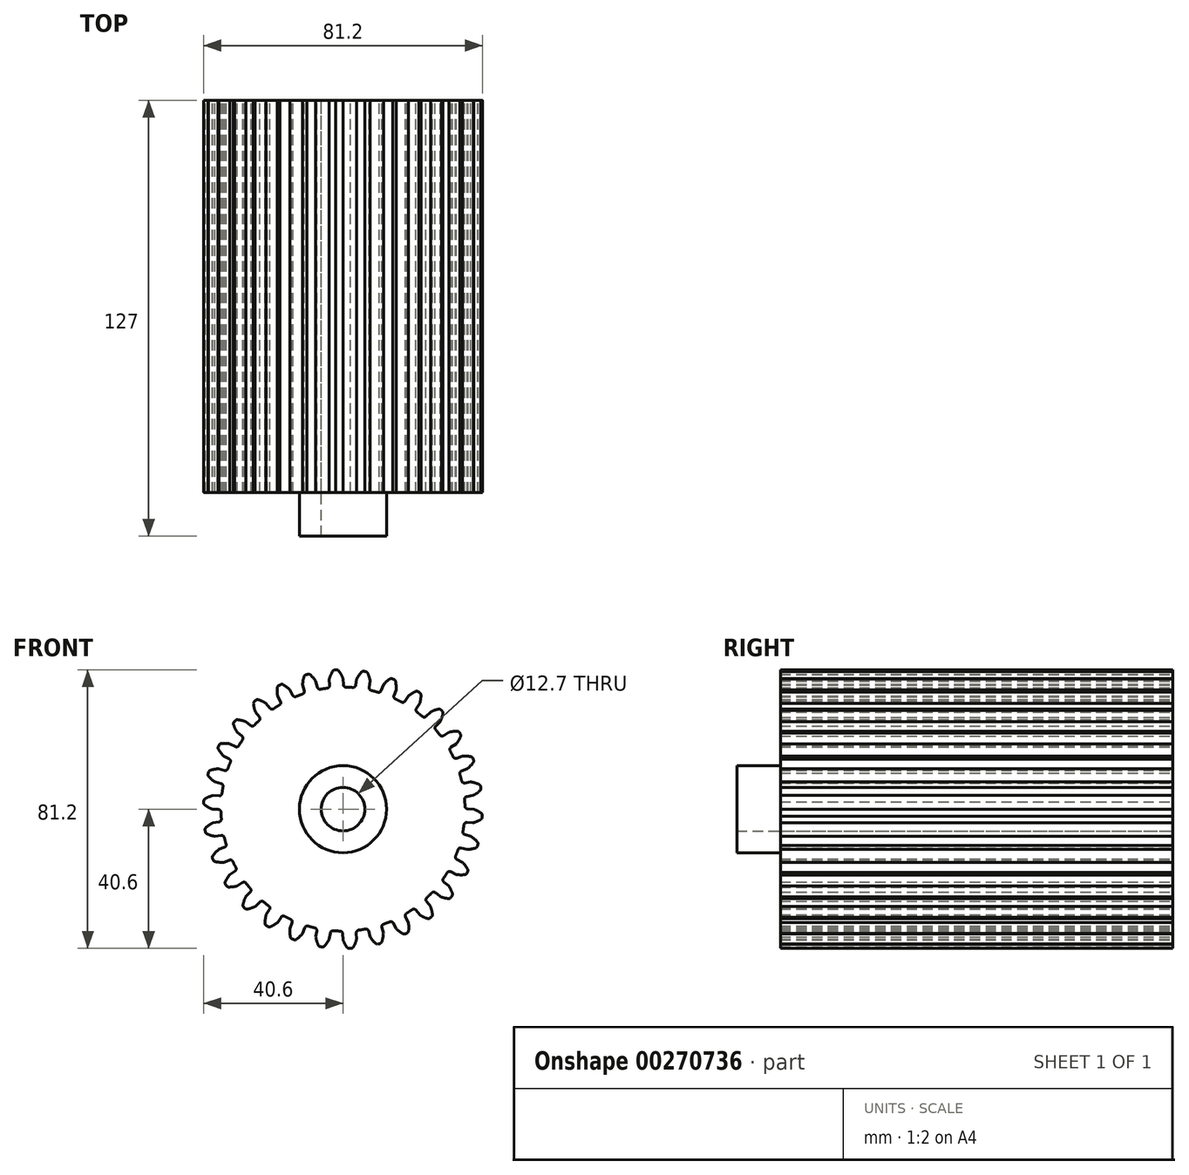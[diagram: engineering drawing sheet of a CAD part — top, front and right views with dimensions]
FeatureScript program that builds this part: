
annotation { "Feature Type Name" : "Feature", "Feature Type Description" : "" }
export const myFeature = defineFeature(function(context is Context, id is Id, definition is map)
    precondition{}
    {
        {
            var Q0;
            Q0=qCreatedBy(makeId("Front.planeOp"),FACE);
            var sketch = newSketch(context, id + "F0", { "sketchPlane" : qUnion([Q0])});
            skArc(sketch, "E0", {"start": v(-4.57, 35.26) * mm, "mid": v(-5.56, 35.12) * mm, "end": v(-6.55, 34.95) * mm});
            skArc(sketch, "E1", {"start": v(0, 38.1) * mm, "mid": v(-0.52, 39.23) * mm, "end": v(-1.18, 40.28) * mm});
            skLineSegment(sketch, "E2", {"start": v(-1.85, 40.6) * mm, "end": v(-2.13, 40.6) * mm});
            skLineSegment(sketch, "E3", {"start": v(0, 38.1) * mm, "end": v(0.1, 36.3) * mm});
            skLineSegment(sketch, "E4.MirrorCS", {"start": v(-2.4, 40.57) * mm, "end": v(-2.13, 40.6) * mm});
            skArc(sketch, "E5.MirrorCS", {"start": v(-3.98, 37.9) * mm, "mid": v(-3.58, 39.07) * mm, "end": v(-3.03, 40.18) * mm});
            skLineSegment(sketch, "E6.MirrorCS", {"start": v(-3.98, 37.9) * mm, "end": v(-3.89, 36.09) * mm});
            skPoint(sketch, "E7.visualSharp", {"position": v(-3.85, 35.35) * mm});
            skArc(sketch, "E7.filletArc", {"start": v(-4.57, 35.26) * mm, "mid": v(-4.07, 35.54) * mm, "end": v(-3.89, 36.09) * mm});
            skPoint(sketch, "E8.visualSharp", {"position": v(0.13, 35.56) * mm});
            skArc(sketch, "E8.filletArc", {"start": v(0.1, 36.3) * mm, "mid": v(0.33, 35.77) * mm, "end": v(0.86, 35.55) * mm});
            skPoint(sketch, "E9.visualSharp", {"position": v(-2.81, 40.54) * mm});
            skArc(sketch, "E9.filletArc", {"start": v(-2.4, 40.57) * mm, "mid": v(-2.77, 40.45) * mm, "end": v(-3.03, 40.18) * mm});
            skPoint(sketch, "E10.visualSharp", {"position": v(-1.44, 40.61) * mm});
            skArc(sketch, "E10.filletArc", {"start": v(-1.18, 40.28) * mm, "mid": v(-1.47, 40.52) * mm, "end": v(-1.85, 40.6) * mm});
            skArc(sketch, "E11.1.0", {"start": v(-11.8, 33.54) * mm, "mid": v(-11.37, 33.92) * mm, "end": v(-11.3, 34.49) * mm});
            skLineSegment(sketch, "E11.1.1", {"start": v(-11.77, 36.24) * mm, "end": v(-11.3, 34.49) * mm});
            skArc(sketch, "E11.1.2", {"start": v(-11.77, 36.24) * mm, "mid": v(-11.63, 37.47) * mm, "end": v(-11.32, 38.67) * mm});
            skArc(sketch, "E11.1.3", {"start": v(-10.79, 39.18) * mm, "mid": v(-11.12, 39) * mm, "end": v(-11.32, 38.67) * mm});
            skLineSegment(sketch, "E11.1.4", {"start": v(-10.79, 39.18) * mm, "end": v(-10.52, 39.26) * mm});
            skLineSegment(sketch, "E11.1.5", {"start": v(-10.25, 39.33) * mm, "end": v(-10.52, 39.26) * mm});
            skArc(sketch, "E11.1.6", {"start": v(-9.53, 39.15) * mm, "mid": v(-9.87, 39.33) * mm, "end": v(-10.25, 39.33) * mm});
            skArc(sketch, "E11.1.7", {"start": v(-7.92, 37.27) * mm, "mid": v(-8.66, 38.26) * mm, "end": v(-9.53, 39.15) * mm});
            skLineSegment(sketch, "E11.1.8", {"start": v(-7.92, 37.27) * mm, "end": v(-7.45, 35.52) * mm});
            skArc(sketch, "E11.1.9", {"start": v(-7.45, 35.52) * mm, "mid": v(-7.11, 35.06) * mm, "end": v(-6.55, 34.95) * mm});
            skArc(sketch, "E11.2.0", {"start": v(-18.52, 30.36) * mm, "mid": v(-18.17, 30.81) * mm, "end": v(-18.23, 31.39) * mm});
            skLineSegment(sketch, "E11.2.1", {"start": v(-19.05, 33) * mm, "end": v(-18.23, 31.39) * mm});
            skArc(sketch, "E11.2.2", {"start": v(-19.05, 33) * mm, "mid": v(-19.16, 34.23) * mm, "end": v(-19.11, 35.47) * mm});
            skArc(sketch, "E11.2.3", {"start": v(-18.7, 36.08) * mm, "mid": v(-18.98, 35.83) * mm, "end": v(-19.11, 35.47) * mm});
            skLineSegment(sketch, "E11.2.4", {"start": v(-18.7, 36.08) * mm, "end": v(-18.45, 36.22) * mm});
            skLineSegment(sketch, "E11.2.5", {"start": v(-18.2, 36.34) * mm, "end": v(-18.45, 36.22) * mm});
            skArc(sketch, "E11.2.6", {"start": v(-17.46, 36.31) * mm, "mid": v(-17.83, 36.42) * mm, "end": v(-18.2, 36.34) * mm});
            skArc(sketch, "E11.2.7", {"start": v(-15.5, 34.8) * mm, "mid": v(-16.43, 35.62) * mm, "end": v(-17.46, 36.31) * mm});
            skLineSegment(sketch, "E11.2.8", {"start": v(-15.5, 34.8) * mm, "end": v(-14.68, 33.2) * mm});
            skArc(sketch, "E11.2.9", {"start": v(-14.68, 33.2) * mm, "mid": v(-14.25, 32.81) * mm, "end": v(-13.67, 32.83) * mm});
            skArc(sketch, "E11.3.0", {"start": v(-24.43, 25.84) * mm, "mid": v(-24.18, 26.36) * mm, "end": v(-24.36, 26.9) * mm});
            skLineSegment(sketch, "E11.3.1", {"start": v(-25.5, 28.31) * mm, "end": v(-24.36, 26.9) * mm});
            skArc(sketch, "E11.3.2", {"start": v(-25.5, 28.31) * mm, "mid": v(-25.86, 29.5) * mm, "end": v(-26.07, 30.72) * mm});
            skArc(sketch, "E11.3.3", {"start": v(-25.8, 31.4) * mm, "mid": v(-26.02, 31.1) * mm, "end": v(-26.07, 30.72) * mm});
            skLineSegment(sketch, "E11.3.4", {"start": v(-25.8, 31.4) * mm, "end": v(-25.58, 31.59) * mm});
            skLineSegment(sketch, "E11.3.5", {"start": v(-25.36, 31.76) * mm, "end": v(-25.58, 31.59) * mm});
            skArc(sketch, "E11.3.6", {"start": v(-24.63, 31.89) * mm, "mid": v(-25, 31.92) * mm, "end": v(-25.36, 31.76) * mm});
            skArc(sketch, "E11.3.7", {"start": v(-22.4, 30.82) * mm, "mid": v(-23.48, 31.43) * mm, "end": v(-24.63, 31.89) * mm});
            skLineSegment(sketch, "E11.3.8", {"start": v(-22.4, 30.82) * mm, "end": v(-21.26, 29.42) * mm});
            skArc(sketch, "E11.3.9", {"start": v(-21.26, 29.42) * mm, "mid": v(-20.76, 29.14) * mm, "end": v(-20.2, 29.27) * mm});
            skArc(sketch, "E11.4.0", {"start": v(-29.27, 20.2) * mm, "mid": v(-29.14, 20.76) * mm, "end": v(-29.42, 21.26) * mm});
            skLineSegment(sketch, "E11.4.1", {"start": v(-30.82, 22.4) * mm, "end": v(-29.42, 21.26) * mm});
            skArc(sketch, "E11.4.2", {"start": v(-30.82, 22.4) * mm, "mid": v(-31.43, 23.48) * mm, "end": v(-31.89, 24.63) * mm});
            skArc(sketch, "E11.4.3", {"start": v(-31.76, 25.36) * mm, "mid": v(-31.92, 25) * mm, "end": v(-31.89, 24.63) * mm});
            skLineSegment(sketch, "E11.4.4", {"start": v(-31.76, 25.36) * mm, "end": v(-31.59, 25.58) * mm});
            skLineSegment(sketch, "E11.4.5", {"start": v(-31.4, 25.8) * mm, "end": v(-31.59, 25.58) * mm});
            skArc(sketch, "E11.4.6", {"start": v(-30.72, 26.07) * mm, "mid": v(-31.1, 26.02) * mm, "end": v(-31.4, 25.8) * mm});
            skArc(sketch, "E11.4.7", {"start": v(-28.31, 25.5) * mm, "mid": v(-29.5, 25.86) * mm, "end": v(-30.72, 26.07) * mm});
            skLineSegment(sketch, "E11.4.8", {"start": v(-28.31, 25.5) * mm, "end": v(-26.9, 24.36) * mm});
            skArc(sketch, "E11.4.9", {"start": v(-26.9, 24.36) * mm, "mid": v(-26.36, 24.18) * mm, "end": v(-25.84, 24.43) * mm});
            skArc(sketch, "E11.5.0", {"start": v(-32.83, 13.67) * mm, "mid": v(-32.81, 14.25) * mm, "end": v(-33.2, 14.68) * mm});
            skLineSegment(sketch, "E11.5.1", {"start": v(-34.8, 15.5) * mm, "end": v(-33.2, 14.68) * mm});
            skArc(sketch, "E11.5.2", {"start": v(-34.8, 15.5) * mm, "mid": v(-35.62, 16.43) * mm, "end": v(-36.31, 17.46) * mm});
            skArc(sketch, "E11.5.3", {"start": v(-36.34, 18.2) * mm, "mid": v(-36.42, 17.83) * mm, "end": v(-36.31, 17.46) * mm});
            skLineSegment(sketch, "E11.5.4", {"start": v(-36.34, 18.2) * mm, "end": v(-36.22, 18.45) * mm});
            skLineSegment(sketch, "E11.5.5", {"start": v(-36.08, 18.7) * mm, "end": v(-36.22, 18.45) * mm});
            skArc(sketch, "E11.5.6", {"start": v(-35.47, 19.11) * mm, "mid": v(-35.83, 18.98) * mm, "end": v(-36.08, 18.7) * mm});
            skArc(sketch, "E11.5.7", {"start": v(-33, 19.05) * mm, "mid": v(-34.23, 19.16) * mm, "end": v(-35.47, 19.11) * mm});
            skLineSegment(sketch, "E11.5.8", {"start": v(-33, 19.05) * mm, "end": v(-31.39, 18.23) * mm});
            skArc(sketch, "E11.5.9", {"start": v(-31.39, 18.23) * mm, "mid": v(-30.81, 18.17) * mm, "end": v(-30.36, 18.52) * mm});
            skArc(sketch, "E11.6.0", {"start": v(-34.95, 6.55) * mm, "mid": v(-35.06, 7.11) * mm, "end": v(-35.52, 7.45) * mm});
            skLineSegment(sketch, "E11.6.1", {"start": v(-37.27, 7.92) * mm, "end": v(-35.52, 7.45) * mm});
            skArc(sketch, "E11.6.2", {"start": v(-37.27, 7.92) * mm, "mid": v(-38.26, 8.66) * mm, "end": v(-39.15, 9.53) * mm});
            skArc(sketch, "E11.6.3", {"start": v(-39.33, 10.25) * mm, "mid": v(-39.33, 9.87) * mm, "end": v(-39.15, 9.53) * mm});
            skLineSegment(sketch, "E11.6.4", {"start": v(-39.33, 10.25) * mm, "end": v(-39.26, 10.52) * mm});
            skLineSegment(sketch, "E11.6.5", {"start": v(-39.18, 10.79) * mm, "end": v(-39.26, 10.52) * mm});
            skArc(sketch, "E11.6.6", {"start": v(-38.67, 11.32) * mm, "mid": v(-39, 11.12) * mm, "end": v(-39.18, 10.79) * mm});
            skArc(sketch, "E11.6.7", {"start": v(-36.24, 11.77) * mm, "mid": v(-37.47, 11.63) * mm, "end": v(-38.67, 11.32) * mm});
            skLineSegment(sketch, "E11.6.8", {"start": v(-36.24, 11.77) * mm, "end": v(-34.49, 11.3) * mm});
            skArc(sketch, "E11.6.9", {"start": v(-34.49, 11.3) * mm, "mid": v(-33.92, 11.37) * mm, "end": v(-33.54, 11.8) * mm});
            skArc(sketch, "E11.7.0", {"start": v(-35.55, -0.86) * mm, "mid": v(-35.77, -0.33) * mm, "end": v(-36.3, -0.1) * mm});
            skLineSegment(sketch, "E11.7.1", {"start": v(-38.1, 0) * mm, "end": v(-36.3, -0.1) * mm});
            skArc(sketch, "E11.7.2", {"start": v(-38.1, 0) * mm, "mid": v(-39.23, 0.52) * mm, "end": v(-40.28, 1.18) * mm});
            skArc(sketch, "E11.7.3", {"start": v(-40.6, 1.85) * mm, "mid": v(-40.52, 1.47) * mm, "end": v(-40.28, 1.18) * mm});
            skLineSegment(sketch, "E11.7.4", {"start": v(-40.6, 1.85) * mm, "end": v(-40.6, 2.13) * mm});
            skLineSegment(sketch, "E11.7.5", {"start": v(-40.57, 2.4) * mm, "end": v(-40.6, 2.13) * mm});
            skArc(sketch, "E11.7.6", {"start": v(-40.18, 3.03) * mm, "mid": v(-40.45, 2.77) * mm, "end": v(-40.57, 2.4) * mm});
            skArc(sketch, "E11.7.7", {"start": v(-37.9, 3.98) * mm, "mid": v(-39.07, 3.58) * mm, "end": v(-40.18, 3.03) * mm});
            skLineSegment(sketch, "E11.7.8", {"start": v(-37.9, 3.98) * mm, "end": v(-36.09, 3.89) * mm});
            skArc(sketch, "E11.7.9", {"start": v(-36.09, 3.89) * mm, "mid": v(-35.54, 4.07) * mm, "end": v(-35.26, 4.57) * mm});
            skArc(sketch, "E11.8.0", {"start": v(-34.6, -8.23) * mm, "mid": v(-34.92, -7.76) * mm, "end": v(-35.48, -7.64) * mm});
            skLineSegment(sketch, "E11.8.1", {"start": v(-37.27, -7.92) * mm, "end": v(-35.48, -7.64) * mm});
            skArc(sketch, "E11.8.2", {"start": v(-37.27, -7.92) * mm, "mid": v(-38.48, -7.65) * mm, "end": v(-39.64, -7.22) * mm});
            skArc(sketch, "E11.8.3", {"start": v(-40.1, -6.63) * mm, "mid": v(-39.94, -6.98) * mm, "end": v(-39.64, -7.22) * mm});
            skLineSegment(sketch, "E11.8.4", {"start": v(-40.1, -6.63) * mm, "end": v(-40.15, -6.36) * mm});
            skLineSegment(sketch, "E11.8.5", {"start": v(-40.18, -6.08) * mm, "end": v(-40.15, -6.36) * mm});
            skArc(sketch, "E11.8.6", {"start": v(-39.93, -5.38) * mm, "mid": v(-40.14, -5.7) * mm, "end": v(-40.18, -6.08) * mm});
            skArc(sketch, "E11.8.7", {"start": v(-37.9, -3.98) * mm, "mid": v(-38.96, -4.62) * mm, "end": v(-39.93, -5.38) * mm});
            skLineSegment(sketch, "E11.8.8", {"start": v(-37.9, -3.98) * mm, "end": v(-36.1, -3.7) * mm});
            skArc(sketch, "E11.8.9", {"start": v(-36.1, -3.7) * mm, "mid": v(-35.61, -3.4) * mm, "end": v(-35.44, -2.86) * mm});
            skArc(sketch, "E11.9.0", {"start": v(-32.13, -15.25) * mm, "mid": v(-32.54, -14.85) * mm, "end": v(-33.12, -14.85) * mm});
            skLineSegment(sketch, "E11.9.1", {"start": v(-34.8, -15.5) * mm, "end": v(-33.12, -14.85) * mm});
            skArc(sketch, "E11.9.2", {"start": v(-34.8, -15.5) * mm, "mid": v(-36.05, -15.48) * mm, "end": v(-37.27, -15.3) * mm});
            skArc(sketch, "E11.9.3", {"start": v(-37.84, -14.83) * mm, "mid": v(-37.62, -15.14) * mm, "end": v(-37.27, -15.3) * mm});
            skLineSegment(sketch, "E11.9.4", {"start": v(-37.84, -14.83) * mm, "end": v(-37.95, -14.57) * mm});
            skLineSegment(sketch, "E11.9.5", {"start": v(-38.04, -14.3) * mm, "end": v(-37.95, -14.57) * mm});
            skArc(sketch, "E11.9.6", {"start": v(-37.94, -13.57) * mm, "mid": v(-38.08, -13.92) * mm, "end": v(-38.04, -14.3) * mm});
            skArc(sketch, "E11.9.7", {"start": v(-36.24, -11.77) * mm, "mid": v(-37.15, -12.62) * mm, "end": v(-37.94, -13.57) * mm});
            skLineSegment(sketch, "E11.9.8", {"start": v(-36.24, -11.77) * mm, "end": v(-34.55, -11.13) * mm});
            skArc(sketch, "E11.9.9", {"start": v(-34.55, -11.13) * mm, "mid": v(-34.12, -10.74) * mm, "end": v(-34.08, -10.17) * mm});
            skArc(sketch, "E11.10.0", {"start": v(-28.25, -21.6) * mm, "mid": v(-28.75, -21.3) * mm, "end": v(-29.3, -21.41) * mm});
            skLineSegment(sketch, "E11.10.1", {"start": v(-30.82, -22.4) * mm, "end": v(-29.3, -21.41) * mm});
            skArc(sketch, "E11.10.2", {"start": v(-30.82, -22.4) * mm, "mid": v(-32.04, -22.64) * mm, "end": v(-33.28, -22.72) * mm});
            skArc(sketch, "E11.10.3", {"start": v(-33.93, -22.37) * mm, "mid": v(-33.65, -22.63) * mm, "end": v(-33.28, -22.72) * mm});
            skLineSegment(sketch, "E11.10.4", {"start": v(-33.93, -22.37) * mm, "end": v(-34.09, -22.14) * mm});
            skLineSegment(sketch, "E11.10.5", {"start": v(-34.24, -21.9) * mm, "end": v(-34.09, -22.14) * mm});
            skArc(sketch, "E11.10.6", {"start": v(-34.29, -21.16) * mm, "mid": v(-34.36, -21.54) * mm, "end": v(-34.24, -21.9) * mm});
            skArc(sketch, "E11.10.7", {"start": v(-33, -19.05) * mm, "mid": v(-33.71, -20.06) * mm, "end": v(-34.29, -21.16) * mm});
            skLineSegment(sketch, "E11.10.8", {"start": v(-33, -19.05) * mm, "end": v(-31.48, -18.07) * mm});
            skArc(sketch, "E11.10.9", {"start": v(-31.48, -18.07) * mm, "mid": v(-31.15, -17.6) * mm, "end": v(-31.22, -17.03) * mm});
            skArc(sketch, "E11.11.0", {"start": v(-23.15, -27) * mm, "mid": v(-23.69, -26.8) * mm, "end": v(-24.22, -27.04) * mm});
            skLineSegment(sketch, "E11.11.1", {"start": v(-25.5, -28.31) * mm, "end": v(-24.22, -27.04) * mm});
            skArc(sketch, "E11.11.2", {"start": v(-25.5, -28.31) * mm, "mid": v(-26.63, -28.8) * mm, "end": v(-27.83, -29.14) * mm});
            skArc(sketch, "E11.11.3", {"start": v(-28.54, -28.94) * mm, "mid": v(-28.2, -29.13) * mm, "end": v(-27.83, -29.14) * mm});
            skLineSegment(sketch, "E11.11.4", {"start": v(-28.54, -28.94) * mm, "end": v(-28.74, -28.74) * mm});
            skLineSegment(sketch, "E11.11.5", {"start": v(-28.94, -28.54) * mm, "end": v(-28.74, -28.74) * mm});
            skArc(sketch, "E11.11.6", {"start": v(-29.14, -27.83) * mm, "mid": v(-29.13, -28.2) * mm, "end": v(-28.94, -28.54) * mm});
            skArc(sketch, "E11.11.7", {"start": v(-28.31, -25.5) * mm, "mid": v(-28.8, -26.63) * mm, "end": v(-29.14, -27.83) * mm});
            skLineSegment(sketch, "E11.11.8", {"start": v(-28.31, -25.5) * mm, "end": v(-27.04, -24.22) * mm});
            skArc(sketch, "E11.11.9", {"start": v(-27.04, -24.22) * mm, "mid": v(-26.8, -23.69) * mm, "end": v(-27, -23.15) * mm});
            skArc(sketch, "E11.12.0", {"start": v(-17.03, -31.22) * mm, "mid": v(-17.6, -31.15) * mm, "end": v(-18.07, -31.48) * mm});
            skLineSegment(sketch, "E11.12.1", {"start": v(-19.05, -33) * mm, "end": v(-18.07, -31.48) * mm});
            skArc(sketch, "E11.12.2", {"start": v(-19.05, -33) * mm, "mid": v(-20.06, -33.71) * mm, "end": v(-21.16, -34.29) * mm});
            skArc(sketch, "E11.12.3", {"start": v(-21.9, -34.24) * mm, "mid": v(-21.54, -34.36) * mm, "end": v(-21.16, -34.29) * mm});
            skLineSegment(sketch, "E11.12.4", {"start": v(-21.9, -34.24) * mm, "end": v(-22.14, -34.09) * mm});
            skLineSegment(sketch, "E11.12.5", {"start": v(-22.37, -33.93) * mm, "end": v(-22.14, -34.09) * mm});
            skArc(sketch, "E11.12.6", {"start": v(-22.72, -33.28) * mm, "mid": v(-22.63, -33.65) * mm, "end": v(-22.37, -33.93) * mm});
            skArc(sketch, "E11.12.7", {"start": v(-22.4, -30.82) * mm, "mid": v(-22.64, -32.04) * mm, "end": v(-22.72, -33.28) * mm});
            skLineSegment(sketch, "E11.12.8", {"start": v(-22.4, -30.82) * mm, "end": v(-21.41, -29.3) * mm});
            skArc(sketch, "E11.12.9", {"start": v(-21.41, -29.3) * mm, "mid": v(-21.3, -28.75) * mm, "end": v(-21.6, -28.25) * mm});
            skArc(sketch, "E11.13.0", {"start": v(-10.17, -34.08) * mm, "mid": v(-10.74, -34.12) * mm, "end": v(-11.13, -34.55) * mm});
            skLineSegment(sketch, "E11.13.1", {"start": v(-11.77, -36.24) * mm, "end": v(-11.13, -34.55) * mm});
            skArc(sketch, "E11.13.2", {"start": v(-11.77, -36.24) * mm, "mid": v(-12.62, -37.15) * mm, "end": v(-13.57, -37.94) * mm});
            skArc(sketch, "E11.13.3", {"start": v(-14.3, -38.04) * mm, "mid": v(-13.92, -38.08) * mm, "end": v(-13.57, -37.94) * mm});
            skLineSegment(sketch, "E11.13.4", {"start": v(-14.3, -38.04) * mm, "end": v(-14.57, -37.95) * mm});
            skLineSegment(sketch, "E11.13.5", {"start": v(-14.83, -37.84) * mm, "end": v(-14.57, -37.95) * mm});
            skArc(sketch, "E11.13.6", {"start": v(-15.3, -37.27) * mm, "mid": v(-15.14, -37.62) * mm, "end": v(-14.83, -37.84) * mm});
            skArc(sketch, "E11.13.7", {"start": v(-15.5, -34.8) * mm, "mid": v(-15.48, -36.05) * mm, "end": v(-15.3, -37.27) * mm});
            skLineSegment(sketch, "E11.13.8", {"start": v(-15.5, -34.8) * mm, "end": v(-14.85, -33.12) * mm});
            skArc(sketch, "E11.13.9", {"start": v(-14.85, -33.12) * mm, "mid": v(-14.85, -32.54) * mm, "end": v(-15.25, -32.13) * mm});
            skArc(sketch, "E11.14.0", {"start": v(-2.86, -35.44) * mm, "mid": v(-3.4, -35.61) * mm, "end": v(-3.7, -36.1) * mm});
            skLineSegment(sketch, "E11.14.1", {"start": v(-3.98, -37.9) * mm, "end": v(-3.7, -36.1) * mm});
            skArc(sketch, "E11.14.2", {"start": v(-3.98, -37.9) * mm, "mid": v(-4.62, -38.96) * mm, "end": v(-5.38, -39.93) * mm});
            skArc(sketch, "E11.14.3", {"start": v(-6.08, -40.18) * mm, "mid": v(-5.7, -40.14) * mm, "end": v(-5.38, -39.93) * mm});
            skLineSegment(sketch, "E11.14.4", {"start": v(-6.08, -40.18) * mm, "end": v(-6.36, -40.15) * mm});
            skLineSegment(sketch, "E11.14.5", {"start": v(-6.63, -40.1) * mm, "end": v(-6.36, -40.15) * mm});
            skArc(sketch, "E11.14.6", {"start": v(-7.22, -39.64) * mm, "mid": v(-6.98, -39.94) * mm, "end": v(-6.63, -40.1) * mm});
            skArc(sketch, "E11.14.7", {"start": v(-7.92, -37.27) * mm, "mid": v(-7.65, -38.48) * mm, "end": v(-7.22, -39.64) * mm});
            skLineSegment(sketch, "E11.14.8", {"start": v(-7.92, -37.27) * mm, "end": v(-7.64, -35.48) * mm});
            skArc(sketch, "E11.14.9", {"start": v(-7.64, -35.48) * mm, "mid": v(-7.76, -34.92) * mm, "end": v(-8.23, -34.6) * mm});
            skArc(sketch, "E11.15.0", {"start": v(4.57, -35.26) * mm, "mid": v(4.07, -35.54) * mm, "end": v(3.89, -36.09) * mm});
            skLineSegment(sketch, "E11.15.1", {"start": v(3.98, -37.9) * mm, "end": v(3.89, -36.09) * mm});
            skArc(sketch, "E11.15.2", {"start": v(3.98, -37.9) * mm, "mid": v(3.58, -39.07) * mm, "end": v(3.03, -40.18) * mm});
            skArc(sketch, "E11.15.3", {"start": v(2.4, -40.57) * mm, "mid": v(2.77, -40.45) * mm, "end": v(3.03, -40.18) * mm});
            skLineSegment(sketch, "E11.15.4", {"start": v(2.4, -40.57) * mm, "end": v(2.13, -40.6) * mm});
            skLineSegment(sketch, "E11.15.5", {"start": v(1.85, -40.6) * mm, "end": v(2.13, -40.6) * mm});
            skArc(sketch, "E11.15.6", {"start": v(1.18, -40.28) * mm, "mid": v(1.47, -40.52) * mm, "end": v(1.85, -40.6) * mm});
            skArc(sketch, "E11.15.7", {"start": v(0, -38.1) * mm, "mid": v(0.52, -39.23) * mm, "end": v(1.18, -40.28) * mm});
            skLineSegment(sketch, "E11.15.8", {"start": v(0, -38.1) * mm, "end": v(-0.1, -36.3) * mm});
            skArc(sketch, "E11.15.9", {"start": v(-0.1, -36.3) * mm, "mid": v(-0.33, -35.77) * mm, "end": v(-0.86, -35.55) * mm});
            skArc(sketch, "E11.16.0", {"start": v(11.8, -33.54) * mm, "mid": v(11.37, -33.92) * mm, "end": v(11.3, -34.49) * mm});
            skLineSegment(sketch, "E11.16.1", {"start": v(11.77, -36.24) * mm, "end": v(11.3, -34.49) * mm});
            skArc(sketch, "E11.16.2", {"start": v(11.77, -36.24) * mm, "mid": v(11.63, -37.47) * mm, "end": v(11.32, -38.67) * mm});
            skArc(sketch, "E11.16.3", {"start": v(10.79, -39.18) * mm, "mid": v(11.12, -39) * mm, "end": v(11.32, -38.67) * mm});
            skLineSegment(sketch, "E11.16.4", {"start": v(10.79, -39.18) * mm, "end": v(10.52, -39.26) * mm});
            skLineSegment(sketch, "E11.16.5", {"start": v(10.25, -39.33) * mm, "end": v(10.52, -39.26) * mm});
            skArc(sketch, "E11.16.6", {"start": v(9.53, -39.15) * mm, "mid": v(9.87, -39.33) * mm, "end": v(10.25, -39.33) * mm});
            skArc(sketch, "E11.16.7", {"start": v(7.92, -37.27) * mm, "mid": v(8.66, -38.26) * mm, "end": v(9.53, -39.15) * mm});
            skLineSegment(sketch, "E11.16.8", {"start": v(7.92, -37.27) * mm, "end": v(7.45, -35.52) * mm});
            skArc(sketch, "E11.16.9", {"start": v(7.45, -35.52) * mm, "mid": v(7.11, -35.06) * mm, "end": v(6.55, -34.95) * mm});
            skArc(sketch, "E11.17.0", {"start": v(18.52, -30.36) * mm, "mid": v(18.17, -30.81) * mm, "end": v(18.23, -31.39) * mm});
            skLineSegment(sketch, "E11.17.1", {"start": v(19.05, -33) * mm, "end": v(18.23, -31.39) * mm});
            skArc(sketch, "E11.17.2", {"start": v(19.05, -33) * mm, "mid": v(19.16, -34.23) * mm, "end": v(19.11, -35.47) * mm});
            skArc(sketch, "E11.17.3", {"start": v(18.7, -36.08) * mm, "mid": v(18.98, -35.83) * mm, "end": v(19.11, -35.47) * mm});
            skLineSegment(sketch, "E11.17.4", {"start": v(18.7, -36.08) * mm, "end": v(18.45, -36.22) * mm});
            skLineSegment(sketch, "E11.17.5", {"start": v(18.2, -36.34) * mm, "end": v(18.45, -36.22) * mm});
            skArc(sketch, "E11.17.6", {"start": v(17.46, -36.31) * mm, "mid": v(17.83, -36.42) * mm, "end": v(18.2, -36.34) * mm});
            skArc(sketch, "E11.17.7", {"start": v(15.5, -34.8) * mm, "mid": v(16.43, -35.62) * mm, "end": v(17.46, -36.31) * mm});
            skLineSegment(sketch, "E11.17.8", {"start": v(15.5, -34.8) * mm, "end": v(14.68, -33.2) * mm});
            skArc(sketch, "E11.17.9", {"start": v(14.68, -33.2) * mm, "mid": v(14.25, -32.81) * mm, "end": v(13.67, -32.83) * mm});
            skArc(sketch, "E11.18.0", {"start": v(24.43, -25.84) * mm, "mid": v(24.18, -26.36) * mm, "end": v(24.36, -26.9) * mm});
            skLineSegment(sketch, "E11.18.1", {"start": v(25.5, -28.31) * mm, "end": v(24.36, -26.9) * mm});
            skArc(sketch, "E11.18.2", {"start": v(25.5, -28.31) * mm, "mid": v(25.86, -29.5) * mm, "end": v(26.07, -30.72) * mm});
            skArc(sketch, "E11.18.3", {"start": v(25.8, -31.4) * mm, "mid": v(26.02, -31.1) * mm, "end": v(26.07, -30.72) * mm});
            skLineSegment(sketch, "E11.18.4", {"start": v(25.8, -31.4) * mm, "end": v(25.58, -31.59) * mm});
            skLineSegment(sketch, "E11.18.5", {"start": v(25.36, -31.76) * mm, "end": v(25.58, -31.59) * mm});
            skArc(sketch, "E11.18.6", {"start": v(24.63, -31.89) * mm, "mid": v(25, -31.92) * mm, "end": v(25.36, -31.76) * mm});
            skArc(sketch, "E11.18.7", {"start": v(22.4, -30.82) * mm, "mid": v(23.48, -31.43) * mm, "end": v(24.63, -31.89) * mm});
            skLineSegment(sketch, "E11.18.8", {"start": v(22.4, -30.82) * mm, "end": v(21.26, -29.42) * mm});
            skArc(sketch, "E11.18.9", {"start": v(21.26, -29.42) * mm, "mid": v(20.76, -29.14) * mm, "end": v(20.2, -29.27) * mm});
            skArc(sketch, "E11.19.0", {"start": v(29.27, -20.2) * mm, "mid": v(29.14, -20.76) * mm, "end": v(29.42, -21.26) * mm});
            skLineSegment(sketch, "E11.19.1", {"start": v(30.82, -22.4) * mm, "end": v(29.42, -21.26) * mm});
            skArc(sketch, "E11.19.2", {"start": v(30.82, -22.4) * mm, "mid": v(31.43, -23.48) * mm, "end": v(31.89, -24.63) * mm});
            skArc(sketch, "E11.19.3", {"start": v(31.76, -25.36) * mm, "mid": v(31.92, -25) * mm, "end": v(31.89, -24.63) * mm});
            skLineSegment(sketch, "E11.19.4", {"start": v(31.76, -25.36) * mm, "end": v(31.59, -25.58) * mm});
            skLineSegment(sketch, "E11.19.5", {"start": v(31.4, -25.8) * mm, "end": v(31.59, -25.58) * mm});
            skArc(sketch, "E11.19.6", {"start": v(30.72, -26.07) * mm, "mid": v(31.1, -26.02) * mm, "end": v(31.4, -25.8) * mm});
            skArc(sketch, "E11.19.7", {"start": v(28.31, -25.5) * mm, "mid": v(29.5, -25.86) * mm, "end": v(30.72, -26.07) * mm});
            skLineSegment(sketch, "E11.19.8", {"start": v(28.31, -25.5) * mm, "end": v(26.9, -24.36) * mm});
            skArc(sketch, "E11.19.9", {"start": v(26.9, -24.36) * mm, "mid": v(26.36, -24.18) * mm, "end": v(25.84, -24.43) * mm});
            skArc(sketch, "E11.20.0", {"start": v(32.83, -13.67) * mm, "mid": v(32.81, -14.25) * mm, "end": v(33.2, -14.68) * mm});
            skLineSegment(sketch, "E11.20.1", {"start": v(34.8, -15.5) * mm, "end": v(33.2, -14.68) * mm});
            skArc(sketch, "E11.20.2", {"start": v(34.8, -15.5) * mm, "mid": v(35.62, -16.43) * mm, "end": v(36.31, -17.46) * mm});
            skArc(sketch, "E11.20.3", {"start": v(36.34, -18.2) * mm, "mid": v(36.42, -17.83) * mm, "end": v(36.31, -17.46) * mm});
            skLineSegment(sketch, "E11.20.4", {"start": v(36.34, -18.2) * mm, "end": v(36.22, -18.45) * mm});
            skLineSegment(sketch, "E11.20.5", {"start": v(36.08, -18.7) * mm, "end": v(36.22, -18.45) * mm});
            skArc(sketch, "E11.20.6", {"start": v(35.47, -19.11) * mm, "mid": v(35.83, -18.98) * mm, "end": v(36.08, -18.7) * mm});
            skArc(sketch, "E11.20.7", {"start": v(33, -19.05) * mm, "mid": v(34.23, -19.16) * mm, "end": v(35.47, -19.11) * mm});
            skLineSegment(sketch, "E11.20.8", {"start": v(33, -19.05) * mm, "end": v(31.39, -18.23) * mm});
            skArc(sketch, "E11.20.9", {"start": v(31.39, -18.23) * mm, "mid": v(30.81, -18.17) * mm, "end": v(30.36, -18.52) * mm});
            skArc(sketch, "E11.21.0", {"start": v(34.95, -6.55) * mm, "mid": v(35.06, -7.11) * mm, "end": v(35.52, -7.45) * mm});
            skLineSegment(sketch, "E11.21.1", {"start": v(37.27, -7.92) * mm, "end": v(35.52, -7.45) * mm});
            skArc(sketch, "E11.21.2", {"start": v(37.27, -7.92) * mm, "mid": v(38.26, -8.66) * mm, "end": v(39.15, -9.53) * mm});
            skArc(sketch, "E11.21.3", {"start": v(39.33, -10.25) * mm, "mid": v(39.33, -9.87) * mm, "end": v(39.15, -9.53) * mm});
            skLineSegment(sketch, "E11.21.4", {"start": v(39.33, -10.25) * mm, "end": v(39.26, -10.52) * mm});
            skLineSegment(sketch, "E11.21.5", {"start": v(39.18, -10.79) * mm, "end": v(39.26, -10.52) * mm});
            skArc(sketch, "E11.21.6", {"start": v(38.67, -11.32) * mm, "mid": v(39, -11.12) * mm, "end": v(39.18, -10.79) * mm});
            skArc(sketch, "E11.21.7", {"start": v(36.24, -11.77) * mm, "mid": v(37.47, -11.63) * mm, "end": v(38.67, -11.32) * mm});
            skLineSegment(sketch, "E11.21.8", {"start": v(36.24, -11.77) * mm, "end": v(34.49, -11.3) * mm});
            skArc(sketch, "E11.21.9", {"start": v(34.49, -11.3) * mm, "mid": v(33.92, -11.37) * mm, "end": v(33.54, -11.8) * mm});
            skArc(sketch, "E11.22.0", {"start": v(35.55, 0.86) * mm, "mid": v(35.77, 0.33) * mm, "end": v(36.3, 0.1) * mm});
            skLineSegment(sketch, "E11.22.1", {"start": v(38.1, 0) * mm, "end": v(36.3, 0.1) * mm});
            skArc(sketch, "E11.22.2", {"start": v(38.1, 0) * mm, "mid": v(39.23, -0.52) * mm, "end": v(40.28, -1.18) * mm});
            skArc(sketch, "E11.22.3", {"start": v(40.6, -1.85) * mm, "mid": v(40.52, -1.47) * mm, "end": v(40.28, -1.18) * mm});
            skLineSegment(sketch, "E11.22.4", {"start": v(40.6, -1.85) * mm, "end": v(40.6, -2.13) * mm});
            skLineSegment(sketch, "E11.22.5", {"start": v(40.57, -2.4) * mm, "end": v(40.6, -2.13) * mm});
            skArc(sketch, "E11.22.6", {"start": v(40.18, -3.03) * mm, "mid": v(40.45, -2.77) * mm, "end": v(40.57, -2.4) * mm});
            skArc(sketch, "E11.22.7", {"start": v(37.9, -3.98) * mm, "mid": v(39.07, -3.58) * mm, "end": v(40.18, -3.03) * mm});
            skLineSegment(sketch, "E11.22.8", {"start": v(37.9, -3.98) * mm, "end": v(36.09, -3.89) * mm});
            skArc(sketch, "E11.22.9", {"start": v(36.09, -3.89) * mm, "mid": v(35.54, -4.07) * mm, "end": v(35.26, -4.57) * mm});
            skArc(sketch, "E11.23.0", {"start": v(34.6, 8.23) * mm, "mid": v(34.92, 7.76) * mm, "end": v(35.48, 7.64) * mm});
            skLineSegment(sketch, "E11.23.1", {"start": v(37.27, 7.92) * mm, "end": v(35.48, 7.64) * mm});
            skArc(sketch, "E11.23.2", {"start": v(37.27, 7.92) * mm, "mid": v(38.48, 7.65) * mm, "end": v(39.64, 7.22) * mm});
            skArc(sketch, "E11.23.3", {"start": v(40.1, 6.63) * mm, "mid": v(39.94, 6.98) * mm, "end": v(39.64, 7.22) * mm});
            skLineSegment(sketch, "E11.23.4", {"start": v(40.1, 6.63) * mm, "end": v(40.15, 6.36) * mm});
            skLineSegment(sketch, "E11.23.5", {"start": v(40.18, 6.08) * mm, "end": v(40.15, 6.36) * mm});
            skArc(sketch, "E11.23.6", {"start": v(39.93, 5.38) * mm, "mid": v(40.14, 5.7) * mm, "end": v(40.18, 6.08) * mm});
            skArc(sketch, "E11.23.7", {"start": v(37.9, 3.98) * mm, "mid": v(38.96, 4.62) * mm, "end": v(39.93, 5.38) * mm});
            skLineSegment(sketch, "E11.23.8", {"start": v(37.9, 3.98) * mm, "end": v(36.1, 3.7) * mm});
            skArc(sketch, "E11.23.9", {"start": v(36.1, 3.7) * mm, "mid": v(35.61, 3.4) * mm, "end": v(35.44, 2.86) * mm});
            skArc(sketch, "E11.24.0", {"start": v(32.13, 15.25) * mm, "mid": v(32.54, 14.85) * mm, "end": v(33.12, 14.85) * mm});
            skLineSegment(sketch, "E11.24.1", {"start": v(34.8, 15.5) * mm, "end": v(33.12, 14.85) * mm});
            skArc(sketch, "E11.24.2", {"start": v(34.8, 15.5) * mm, "mid": v(36.05, 15.48) * mm, "end": v(37.27, 15.3) * mm});
            skArc(sketch, "E11.24.3", {"start": v(37.84, 14.83) * mm, "mid": v(37.62, 15.14) * mm, "end": v(37.27, 15.3) * mm});
            skLineSegment(sketch, "E11.24.4", {"start": v(37.84, 14.83) * mm, "end": v(37.95, 14.57) * mm});
            skLineSegment(sketch, "E11.24.5", {"start": v(38.04, 14.3) * mm, "end": v(37.95, 14.57) * mm});
            skArc(sketch, "E11.24.6", {"start": v(37.94, 13.57) * mm, "mid": v(38.08, 13.92) * mm, "end": v(38.04, 14.3) * mm});
            skArc(sketch, "E11.24.7", {"start": v(36.24, 11.77) * mm, "mid": v(37.15, 12.62) * mm, "end": v(37.94, 13.57) * mm});
            skLineSegment(sketch, "E11.24.8", {"start": v(36.24, 11.77) * mm, "end": v(34.55, 11.13) * mm});
            skArc(sketch, "E11.24.9", {"start": v(34.55, 11.13) * mm, "mid": v(34.12, 10.74) * mm, "end": v(34.08, 10.17) * mm});
            skArc(sketch, "E11.25.0", {"start": v(28.25, 21.6) * mm, "mid": v(28.75, 21.3) * mm, "end": v(29.3, 21.41) * mm});
            skLineSegment(sketch, "E11.25.1", {"start": v(30.82, 22.4) * mm, "end": v(29.3, 21.41) * mm});
            skArc(sketch, "E11.25.2", {"start": v(30.82, 22.4) * mm, "mid": v(32.04, 22.64) * mm, "end": v(33.28, 22.72) * mm});
            skArc(sketch, "E11.25.3", {"start": v(33.93, 22.37) * mm, "mid": v(33.65, 22.63) * mm, "end": v(33.28, 22.72) * mm});
            skLineSegment(sketch, "E11.25.4", {"start": v(33.93, 22.37) * mm, "end": v(34.09, 22.14) * mm});
            skLineSegment(sketch, "E11.25.5", {"start": v(34.24, 21.9) * mm, "end": v(34.09, 22.14) * mm});
            skArc(sketch, "E11.25.6", {"start": v(34.29, 21.16) * mm, "mid": v(34.36, 21.54) * mm, "end": v(34.24, 21.9) * mm});
            skArc(sketch, "E11.25.7", {"start": v(33, 19.05) * mm, "mid": v(33.71, 20.06) * mm, "end": v(34.29, 21.16) * mm});
            skLineSegment(sketch, "E11.25.8", {"start": v(33, 19.05) * mm, "end": v(31.48, 18.07) * mm});
            skArc(sketch, "E11.25.9", {"start": v(31.48, 18.07) * mm, "mid": v(31.15, 17.6) * mm, "end": v(31.22, 17.03) * mm});
            skArc(sketch, "E11.26.0", {"start": v(23.15, 27) * mm, "mid": v(23.69, 26.8) * mm, "end": v(24.22, 27.04) * mm});
            skLineSegment(sketch, "E11.26.1", {"start": v(25.5, 28.31) * mm, "end": v(24.22, 27.04) * mm});
            skArc(sketch, "E11.26.2", {"start": v(25.5, 28.31) * mm, "mid": v(26.63, 28.8) * mm, "end": v(27.83, 29.14) * mm});
            skArc(sketch, "E11.26.3", {"start": v(28.54, 28.94) * mm, "mid": v(28.2, 29.13) * mm, "end": v(27.83, 29.14) * mm});
            skLineSegment(sketch, "E11.26.4", {"start": v(28.54, 28.94) * mm, "end": v(28.74, 28.74) * mm});
            skLineSegment(sketch, "E11.26.5", {"start": v(28.94, 28.54) * mm, "end": v(28.74, 28.74) * mm});
            skArc(sketch, "E11.26.6", {"start": v(29.14, 27.83) * mm, "mid": v(29.13, 28.2) * mm, "end": v(28.94, 28.54) * mm});
            skArc(sketch, "E11.26.7", {"start": v(28.31, 25.5) * mm, "mid": v(28.8, 26.63) * mm, "end": v(29.14, 27.83) * mm});
            skLineSegment(sketch, "E11.26.8", {"start": v(28.31, 25.5) * mm, "end": v(27.04, 24.22) * mm});
            skArc(sketch, "E11.26.9", {"start": v(27.04, 24.22) * mm, "mid": v(26.8, 23.69) * mm, "end": v(27, 23.15) * mm});
            skArc(sketch, "E11.27.0", {"start": v(17.03, 31.22) * mm, "mid": v(17.6, 31.15) * mm, "end": v(18.07, 31.48) * mm});
            skLineSegment(sketch, "E11.27.1", {"start": v(19.05, 33) * mm, "end": v(18.07, 31.48) * mm});
            skArc(sketch, "E11.27.2", {"start": v(19.05, 33) * mm, "mid": v(20.06, 33.71) * mm, "end": v(21.16, 34.29) * mm});
            skArc(sketch, "E11.27.3", {"start": v(21.9, 34.24) * mm, "mid": v(21.54, 34.36) * mm, "end": v(21.16, 34.29) * mm});
            skLineSegment(sketch, "E11.27.4", {"start": v(21.9, 34.24) * mm, "end": v(22.14, 34.09) * mm});
            skLineSegment(sketch, "E11.27.5", {"start": v(22.37, 33.93) * mm, "end": v(22.14, 34.09) * mm});
            skArc(sketch, "E11.27.6", {"start": v(22.72, 33.28) * mm, "mid": v(22.63, 33.65) * mm, "end": v(22.37, 33.93) * mm});
            skArc(sketch, "E11.27.7", {"start": v(22.4, 30.82) * mm, "mid": v(22.64, 32.04) * mm, "end": v(22.72, 33.28) * mm});
            skLineSegment(sketch, "E11.27.8", {"start": v(22.4, 30.82) * mm, "end": v(21.41, 29.3) * mm});
            skArc(sketch, "E11.27.9", {"start": v(21.41, 29.3) * mm, "mid": v(21.3, 28.75) * mm, "end": v(21.6, 28.25) * mm});
            skArc(sketch, "E11.28.0", {"start": v(10.17, 34.08) * mm, "mid": v(10.74, 34.12) * mm, "end": v(11.13, 34.55) * mm});
            skLineSegment(sketch, "E11.28.1", {"start": v(11.77, 36.24) * mm, "end": v(11.13, 34.55) * mm});
            skArc(sketch, "E11.28.2", {"start": v(11.77, 36.24) * mm, "mid": v(12.62, 37.15) * mm, "end": v(13.57, 37.94) * mm});
            skArc(sketch, "E11.28.3", {"start": v(14.3, 38.04) * mm, "mid": v(13.92, 38.08) * mm, "end": v(13.57, 37.94) * mm});
            skLineSegment(sketch, "E11.28.4", {"start": v(14.3, 38.04) * mm, "end": v(14.57, 37.95) * mm});
            skLineSegment(sketch, "E11.28.5", {"start": v(14.83, 37.84) * mm, "end": v(14.57, 37.95) * mm});
            skArc(sketch, "E11.28.6", {"start": v(15.3, 37.27) * mm, "mid": v(15.14, 37.62) * mm, "end": v(14.83, 37.84) * mm});
            skArc(sketch, "E11.28.7", {"start": v(15.5, 34.8) * mm, "mid": v(15.48, 36.05) * mm, "end": v(15.3, 37.27) * mm});
            skLineSegment(sketch, "E11.28.8", {"start": v(15.5, 34.8) * mm, "end": v(14.85, 33.12) * mm});
            skArc(sketch, "E11.28.9", {"start": v(14.85, 33.12) * mm, "mid": v(14.85, 32.54) * mm, "end": v(15.25, 32.13) * mm});
            skArc(sketch, "E11.29.0", {"start": v(2.86, 35.44) * mm, "mid": v(3.4, 35.61) * mm, "end": v(3.7, 36.1) * mm});
            skLineSegment(sketch, "E11.29.1", {"start": v(3.98, 37.9) * mm, "end": v(3.7, 36.1) * mm});
            skArc(sketch, "E11.29.2", {"start": v(3.98, 37.9) * mm, "mid": v(4.62, 38.96) * mm, "end": v(5.38, 39.93) * mm});
            skArc(sketch, "E11.29.3", {"start": v(6.08, 40.18) * mm, "mid": v(5.7, 40.14) * mm, "end": v(5.38, 39.93) * mm});
            skLineSegment(sketch, "E11.29.4", {"start": v(6.08, 40.18) * mm, "end": v(6.36, 40.15) * mm});
            skLineSegment(sketch, "E11.29.5", {"start": v(6.63, 40.1) * mm, "end": v(6.36, 40.15) * mm});
            skArc(sketch, "E11.29.6", {"start": v(7.22, 39.64) * mm, "mid": v(6.98, 39.94) * mm, "end": v(6.63, 40.1) * mm});
            skArc(sketch, "E11.29.7", {"start": v(7.92, 37.27) * mm, "mid": v(7.65, 38.48) * mm, "end": v(7.22, 39.64) * mm});
            skLineSegment(sketch, "E11.29.8", {"start": v(7.92, 37.27) * mm, "end": v(7.64, 35.48) * mm});
            skArc(sketch, "E11.29.9", {"start": v(7.64, 35.48) * mm, "mid": v(7.76, 34.92) * mm, "end": v(8.23, 34.6) * mm});
            skArc(sketch, "E12.trimOffspring", {"start": v(2.86, 35.44) * mm, "mid": v(1.86, 35.51) * mm, "end": v(0.86, 35.55) * mm});
            skArc(sketch, "E13.trimOffspring", {"start": v(10.17, 34.08) * mm, "mid": v(9.2, 34.35) * mm, "end": v(8.23, 34.6) * mm});
            skArc(sketch, "E14.trimOffspring", {"start": v(17.03, 31.22) * mm, "mid": v(16.14, 31.68) * mm, "end": v(15.25, 32.13) * mm});
            skArc(sketch, "E15.trimOffspring", {"start": v(23.15, 27) * mm, "mid": v(22.38, 27.64) * mm, "end": v(21.6, 28.25) * mm});
            skArc(sketch, "E16.trimOffspring", {"start": v(28.25, 21.6) * mm, "mid": v(27.64, 22.38) * mm, "end": v(27, 23.15) * mm});
            skArc(sketch, "E17.trimOffspring", {"start": v(32.13, 15.25) * mm, "mid": v(31.68, 16.14) * mm, "end": v(31.22, 17.03) * mm});
            skArc(sketch, "E18.trimOffspring", {"start": v(34.6, 8.23) * mm, "mid": v(34.35, 9.2) * mm, "end": v(34.08, 10.17) * mm});
            skArc(sketch, "E19.trimOffspring", {"start": v(35.55, 0.86) * mm, "mid": v(35.51, 1.86) * mm, "end": v(35.44, 2.86) * mm});
            skArc(sketch, "E20.trimOffspring", {"start": v(34.95, -6.55) * mm, "mid": v(35.12, -5.56) * mm, "end": v(35.26, -4.57) * mm});
            skArc(sketch, "E21.trimOffspring", {"start": v(32.83, -13.67) * mm, "mid": v(33.2, -12.74) * mm, "end": v(33.54, -11.8) * mm});
            skArc(sketch, "E22.trimOffspring", {"start": v(29.27, -20.2) * mm, "mid": v(29.82, -19.37) * mm, "end": v(30.36, -18.52) * mm});
            skArc(sketch, "E23.trimOffspring", {"start": v(24.43, -25.84) * mm, "mid": v(25.14, -25.14) * mm, "end": v(25.84, -24.43) * mm});
            skArc(sketch, "E24.trimOffspring", {"start": v(18.52, -30.36) * mm, "mid": v(19.37, -29.82) * mm, "end": v(20.2, -29.27) * mm});
            skArc(sketch, "E25.trimOffspring", {"start": v(11.8, -33.54) * mm, "mid": v(12.74, -33.2) * mm, "end": v(13.67, -32.83) * mm});
            skArc(sketch, "E26.trimOffspring", {"start": v(4.57, -35.26) * mm, "mid": v(5.56, -35.12) * mm, "end": v(6.55, -34.95) * mm});
            skArc(sketch, "E27.trimOffspring", {"start": v(-2.86, -35.44) * mm, "mid": v(-1.86, -35.51) * mm, "end": v(-0.86, -35.55) * mm});
            skArc(sketch, "E28.trimOffspring", {"start": v(-10.17, -34.08) * mm, "mid": v(-9.2, -34.35) * mm, "end": v(-8.23, -34.6) * mm});
            skArc(sketch, "E29.trimOffspring", {"start": v(-17.03, -31.22) * mm, "mid": v(-16.14, -31.68) * mm, "end": v(-15.25, -32.13) * mm});
            skArc(sketch, "E30.trimOffspring", {"start": v(-23.15, -27) * mm, "mid": v(-22.38, -27.64) * mm, "end": v(-21.6, -28.25) * mm});
            skArc(sketch, "E31.trimOffspring", {"start": v(-28.25, -21.6) * mm, "mid": v(-27.64, -22.38) * mm, "end": v(-27, -23.15) * mm});
            skArc(sketch, "E32.trimOffspring", {"start": v(-32.13, -15.25) * mm, "mid": v(-31.68, -16.14) * mm, "end": v(-31.22, -17.03) * mm});
            skArc(sketch, "E33.trimOffspring", {"start": v(-34.6, -8.23) * mm, "mid": v(-34.35, -9.2) * mm, "end": v(-34.08, -10.17) * mm});
            skArc(sketch, "E34.trimOffspring", {"start": v(-35.55, -0.86) * mm, "mid": v(-35.51, -1.86) * mm, "end": v(-35.44, -2.86) * mm});
            skArc(sketch, "E35.trimOffspring", {"start": v(-34.95, 6.55) * mm, "mid": v(-35.12, 5.56) * mm, "end": v(-35.26, 4.57) * mm});
            skArc(sketch, "E36.trimOffspring", {"start": v(-24.43, 25.84) * mm, "mid": v(-25.14, 25.14) * mm, "end": v(-25.84, 24.43) * mm});
            skArc(sketch, "E37.trimOffspring", {"start": v(-18.52, 30.36) * mm, "mid": v(-19.37, 29.82) * mm, "end": v(-20.2, 29.27) * mm});
            skArc(sketch, "E38.trimOffspring", {"start": v(-29.27, 20.2) * mm, "mid": v(-29.82, 19.37) * mm, "end": v(-30.36, 18.52) * mm});
            skArc(sketch, "E39.trimOffspring", {"start": v(-32.83, 13.67) * mm, "mid": v(-33.2, 12.74) * mm, "end": v(-33.54, 11.8) * mm});
            skArc(sketch, "E40.trimOffspring", {"start": v(-11.8, 33.54) * mm, "mid": v(-12.74, 33.2) * mm, "end": v(-13.67, 32.83) * mm});
            skCircle(sketch, "E41", {"center": v(0, 0) * mm, "radius": 6.35 * mm});
            skSolve(sketch);
        }
        {
            var Q0;
            Q0 = qSketchRegion(id + "F0", true);
            extrude(context, id + "F1", {"entities" : qUnion([Q0]), "depth" : 114.3 * mm});
        }
        {
            var Q0;
            Q0=makeQuery(id+"F1.opExtrude","CAP_FACE",FACE,{"disambiguationData":[OSD([sQuery(id+"F0.wireOp",EDGE,"E0"),sQuery(id+"F0.wireOp",EDGE,"E1"),sQuery(id+"F0.wireOp",EDGE,"E2"),sQuery(id+"F0.wireOp",EDGE,"E3"),sQuery(id+"F0.wireOp",EDGE,"E4.MirrorCS"),sQuery(id+"F0.wireOp",EDGE,"E5.MirrorCS"),sQuery(id+"F0.wireOp",EDGE,"E6.MirrorCS"),sQuery(id+"F0.wireOp",EDGE,"E7.filletArc"),sQuery(id+"F0.wireOp",EDGE,"E8.filletArc"),sQuery(id+"F0.wireOp",EDGE,"E9.filletArc"),sQuery(id+"F0.wireOp",EDGE,"E10.filletArc"),sQuery(id+"F0.wireOp",EDGE,"E11.1.0"),sQuery(id+"F0.wireOp",EDGE,"E11.1.1"),sQuery(id+"F0.wireOp",EDGE,"E11.1.2"),sQuery(id+"F0.wireOp",EDGE,"E11.1.3"),sQuery(id+"F0.wireOp",EDGE,"E11.1.4"),sQuery(id+"F0.wireOp",EDGE,"E11.1.5"),sQuery(id+"F0.wireOp",EDGE,"E11.1.6"),sQuery(id+"F0.wireOp",EDGE,"E11.1.7"),sQuery(id+"F0.wireOp",EDGE,"E11.1.8"),sQuery(id+"F0.wireOp",EDGE,"E11.1.9"),sQuery(id+"F0.wireOp",EDGE,"E11.2.0"),sQuery(id+"F0.wireOp",EDGE,"E11.2.1"),sQuery(id+"F0.wireOp",EDGE,"E11.2.2"),sQuery(id+"F0.wireOp",EDGE,"E11.2.3"),sQuery(id+"F0.wireOp",EDGE,"E11.2.4"),sQuery(id+"F0.wireOp",EDGE,"E11.2.5"),sQuery(id+"F0.wireOp",EDGE,"E11.2.6"),sQuery(id+"F0.wireOp",EDGE,"E11.2.7"),sQuery(id+"F0.wireOp",EDGE,"E11.2.8"),sQuery(id+"F0.wireOp",EDGE,"E11.2.9"),sQuery(id+"F0.wireOp",EDGE,"E11.3.0"),sQuery(id+"F0.wireOp",EDGE,"E11.3.1"),sQuery(id+"F0.wireOp",EDGE,"E11.3.2"),sQuery(id+"F0.wireOp",EDGE,"E11.3.3"),sQuery(id+"F0.wireOp",EDGE,"E11.3.4"),sQuery(id+"F0.wireOp",EDGE,"E11.3.5"),sQuery(id+"F0.wireOp",EDGE,"E11.3.6"),sQuery(id+"F0.wireOp",EDGE,"E11.3.7"),sQuery(id+"F0.wireOp",EDGE,"E11.3.8"),sQuery(id+"F0.wireOp",EDGE,"E11.3.9"),sQuery(id+"F0.wireOp",EDGE,"E11.4.0"),sQuery(id+"F0.wireOp",EDGE,"E11.4.1"),sQuery(id+"F0.wireOp",EDGE,"E11.4.2"),sQuery(id+"F0.wireOp",EDGE,"E11.4.3"),sQuery(id+"F0.wireOp",EDGE,"E11.4.4"),sQuery(id+"F0.wireOp",EDGE,"E11.4.5"),sQuery(id+"F0.wireOp",EDGE,"E11.4.6"),sQuery(id+"F0.wireOp",EDGE,"E11.4.7"),sQuery(id+"F0.wireOp",EDGE,"E11.4.8"),sQuery(id+"F0.wireOp",EDGE,"E11.4.9"),sQuery(id+"F0.wireOp",EDGE,"E11.5.0"),sQuery(id+"F0.wireOp",EDGE,"E11.5.1"),sQuery(id+"F0.wireOp",EDGE,"E11.5.2"),sQuery(id+"F0.wireOp",EDGE,"E11.5.3"),sQuery(id+"F0.wireOp",EDGE,"E11.5.4"),sQuery(id+"F0.wireOp",EDGE,"E11.5.5"),sQuery(id+"F0.wireOp",EDGE,"E11.5.6"),sQuery(id+"F0.wireOp",EDGE,"E11.5.7"),sQuery(id+"F0.wireOp",EDGE,"E11.5.8"),sQuery(id+"F0.wireOp",EDGE,"E11.5.9"),sQuery(id+"F0.wireOp",EDGE,"E11.6.0"),sQuery(id+"F0.wireOp",EDGE,"E11.6.1"),sQuery(id+"F0.wireOp",EDGE,"E11.6.2"),sQuery(id+"F0.wireOp",EDGE,"E11.6.3"),sQuery(id+"F0.wireOp",EDGE,"E11.6.4"),sQuery(id+"F0.wireOp",EDGE,"E11.6.5"),sQuery(id+"F0.wireOp",EDGE,"E11.6.6"),sQuery(id+"F0.wireOp",EDGE,"E11.6.7"),sQuery(id+"F0.wireOp",EDGE,"E11.6.8"),sQuery(id+"F0.wireOp",EDGE,"E11.6.9"),sQuery(id+"F0.wireOp",EDGE,"E11.7.0"),sQuery(id+"F0.wireOp",EDGE,"E11.7.1"),sQuery(id+"F0.wireOp",EDGE,"E11.7.2"),sQuery(id+"F0.wireOp",EDGE,"E11.7.3"),sQuery(id+"F0.wireOp",EDGE,"E11.7.4"),sQuery(id+"F0.wireOp",EDGE,"E11.7.5"),sQuery(id+"F0.wireOp",EDGE,"E11.7.6"),sQuery(id+"F0.wireOp",EDGE,"E11.7.7"),sQuery(id+"F0.wireOp",EDGE,"E11.7.8"),sQuery(id+"F0.wireOp",EDGE,"E11.7.9"),sQuery(id+"F0.wireOp",EDGE,"E11.8.0"),sQuery(id+"F0.wireOp",EDGE,"E11.8.1"),sQuery(id+"F0.wireOp",EDGE,"E11.8.2"),sQuery(id+"F0.wireOp",EDGE,"E11.8.3"),sQuery(id+"F0.wireOp",EDGE,"E11.8.4"),sQuery(id+"F0.wireOp",EDGE,"E11.8.5"),sQuery(id+"F0.wireOp",EDGE,"E11.8.6"),sQuery(id+"F0.wireOp",EDGE,"E11.8.7"),sQuery(id+"F0.wireOp",EDGE,"E11.8.8"),sQuery(id+"F0.wireOp",EDGE,"E11.8.9"),sQuery(id+"F0.wireOp",EDGE,"E11.9.0"),sQuery(id+"F0.wireOp",EDGE,"E11.9.1"),sQuery(id+"F0.wireOp",EDGE,"E11.9.2"),sQuery(id+"F0.wireOp",EDGE,"E11.9.3"),sQuery(id+"F0.wireOp",EDGE,"E11.9.4"),sQuery(id+"F0.wireOp",EDGE,"E11.9.5"),sQuery(id+"F0.wireOp",EDGE,"E11.9.6"),sQuery(id+"F0.wireOp",EDGE,"E11.9.7"),sQuery(id+"F0.wireOp",EDGE,"E11.9.8"),sQuery(id+"F0.wireOp",EDGE,"E11.9.9"),sQuery(id+"F0.wireOp",EDGE,"E11.10.0"),sQuery(id+"F0.wireOp",EDGE,"E11.10.1"),sQuery(id+"F0.wireOp",EDGE,"E11.10.2"),sQuery(id+"F0.wireOp",EDGE,"E11.10.3"),sQuery(id+"F0.wireOp",EDGE,"E11.10.4"),sQuery(id+"F0.wireOp",EDGE,"E11.10.5"),sQuery(id+"F0.wireOp",EDGE,"E11.10.6"),sQuery(id+"F0.wireOp",EDGE,"E11.10.7"),sQuery(id+"F0.wireOp",EDGE,"E11.10.8"),sQuery(id+"F0.wireOp",EDGE,"E11.10.9"),sQuery(id+"F0.wireOp",EDGE,"E11.11.0"),sQuery(id+"F0.wireOp",EDGE,"E11.11.1"),sQuery(id+"F0.wireOp",EDGE,"E11.11.2"),sQuery(id+"F0.wireOp",EDGE,"E11.11.3"),sQuery(id+"F0.wireOp",EDGE,"E11.11.4"),sQuery(id+"F0.wireOp",EDGE,"E11.11.5"),sQuery(id+"F0.wireOp",EDGE,"E11.11.6"),sQuery(id+"F0.wireOp",EDGE,"E11.11.7"),sQuery(id+"F0.wireOp",EDGE,"E11.11.8"),sQuery(id+"F0.wireOp",EDGE,"E11.11.9"),sQuery(id+"F0.wireOp",EDGE,"E11.12.0"),sQuery(id+"F0.wireOp",EDGE,"E11.12.1"),sQuery(id+"F0.wireOp",EDGE,"E11.12.2"),sQuery(id+"F0.wireOp",EDGE,"E11.12.3"),sQuery(id+"F0.wireOp",EDGE,"E11.12.4"),sQuery(id+"F0.wireOp",EDGE,"E11.12.5"),sQuery(id+"F0.wireOp",EDGE,"E11.12.6"),sQuery(id+"F0.wireOp",EDGE,"E11.12.7"),sQuery(id+"F0.wireOp",EDGE,"E11.12.8"),sQuery(id+"F0.wireOp",EDGE,"E11.12.9"),sQuery(id+"F0.wireOp",EDGE,"E11.13.0"),sQuery(id+"F0.wireOp",EDGE,"E11.13.1"),sQuery(id+"F0.wireOp",EDGE,"E11.13.2"),sQuery(id+"F0.wireOp",EDGE,"E11.13.3"),sQuery(id+"F0.wireOp",EDGE,"E11.13.4"),sQuery(id+"F0.wireOp",EDGE,"E11.13.5"),sQuery(id+"F0.wireOp",EDGE,"E11.13.6"),sQuery(id+"F0.wireOp",EDGE,"E11.13.7"),sQuery(id+"F0.wireOp",EDGE,"E11.13.8"),sQuery(id+"F0.wireOp",EDGE,"E11.13.9"),sQuery(id+"F0.wireOp",EDGE,"E11.14.0"),sQuery(id+"F0.wireOp",EDGE,"E11.14.1"),sQuery(id+"F0.wireOp",EDGE,"E11.14.2"),sQuery(id+"F0.wireOp",EDGE,"E11.14.3"),sQuery(id+"F0.wireOp",EDGE,"E11.14.4"),sQuery(id+"F0.wireOp",EDGE,"E11.14.5"),sQuery(id+"F0.wireOp",EDGE,"E11.14.6"),sQuery(id+"F0.wireOp",EDGE,"E11.14.7"),sQuery(id+"F0.wireOp",EDGE,"E11.14.8"),sQuery(id+"F0.wireOp",EDGE,"E11.14.9"),sQuery(id+"F0.wireOp",EDGE,"E11.15.0"),sQuery(id+"F0.wireOp",EDGE,"E11.15.1"),sQuery(id+"F0.wireOp",EDGE,"E11.15.2"),sQuery(id+"F0.wireOp",EDGE,"E11.15.3"),sQuery(id+"F0.wireOp",EDGE,"E11.15.4"),sQuery(id+"F0.wireOp",EDGE,"E11.15.5"),sQuery(id+"F0.wireOp",EDGE,"E11.15.6"),sQuery(id+"F0.wireOp",EDGE,"E11.15.7"),sQuery(id+"F0.wireOp",EDGE,"E11.15.8"),sQuery(id+"F0.wireOp",EDGE,"E11.15.9"),sQuery(id+"F0.wireOp",EDGE,"E11.16.0"),sQuery(id+"F0.wireOp",EDGE,"E11.16.1"),sQuery(id+"F0.wireOp",EDGE,"E11.16.2"),sQuery(id+"F0.wireOp",EDGE,"E11.16.3"),sQuery(id+"F0.wireOp",EDGE,"E11.16.4"),sQuery(id+"F0.wireOp",EDGE,"E11.16.5"),sQuery(id+"F0.wireOp",EDGE,"E11.16.6"),sQuery(id+"F0.wireOp",EDGE,"E11.16.7"),sQuery(id+"F0.wireOp",EDGE,"E11.16.8"),sQuery(id+"F0.wireOp",EDGE,"E11.16.9"),sQuery(id+"F0.wireOp",EDGE,"E11.17.0"),sQuery(id+"F0.wireOp",EDGE,"E11.17.1"),sQuery(id+"F0.wireOp",EDGE,"E11.17.2"),sQuery(id+"F0.wireOp",EDGE,"E11.17.3"),sQuery(id+"F0.wireOp",EDGE,"E11.17.4"),sQuery(id+"F0.wireOp",EDGE,"E11.17.5"),sQuery(id+"F0.wireOp",EDGE,"E11.17.6"),sQuery(id+"F0.wireOp",EDGE,"E11.17.7"),sQuery(id+"F0.wireOp",EDGE,"E11.17.8"),sQuery(id+"F0.wireOp",EDGE,"E11.17.9"),sQuery(id+"F0.wireOp",EDGE,"E11.18.0"),sQuery(id+"F0.wireOp",EDGE,"E11.18.1"),sQuery(id+"F0.wireOp",EDGE,"E11.18.2"),sQuery(id+"F0.wireOp",EDGE,"E11.18.3"),sQuery(id+"F0.wireOp",EDGE,"E11.18.4"),sQuery(id+"F0.wireOp",EDGE,"E11.18.5"),sQuery(id+"F0.wireOp",EDGE,"E11.18.6"),sQuery(id+"F0.wireOp",EDGE,"E11.18.7"),sQuery(id+"F0.wireOp",EDGE,"E11.18.8"),sQuery(id+"F0.wireOp",EDGE,"E11.18.9"),sQuery(id+"F0.wireOp",EDGE,"E11.19.0"),sQuery(id+"F0.wireOp",EDGE,"E11.19.1"),sQuery(id+"F0.wireOp",EDGE,"E11.19.2"),sQuery(id+"F0.wireOp",EDGE,"E11.19.3"),sQuery(id+"F0.wireOp",EDGE,"E11.19.4"),sQuery(id+"F0.wireOp",EDGE,"E11.19.5"),sQuery(id+"F0.wireOp",EDGE,"E11.19.6"),sQuery(id+"F0.wireOp",EDGE,"E11.19.7"),sQuery(id+"F0.wireOp",EDGE,"E11.19.8"),sQuery(id+"F0.wireOp",EDGE,"E11.19.9"),sQuery(id+"F0.wireOp",EDGE,"E11.20.0"),sQuery(id+"F0.wireOp",EDGE,"E11.20.1"),sQuery(id+"F0.wireOp",EDGE,"E11.20.2"),sQuery(id+"F0.wireOp",EDGE,"E11.20.3"),sQuery(id+"F0.wireOp",EDGE,"E11.20.4"),sQuery(id+"F0.wireOp",EDGE,"E11.20.5"),sQuery(id+"F0.wireOp",EDGE,"E11.20.6"),sQuery(id+"F0.wireOp",EDGE,"E11.20.7"),sQuery(id+"F0.wireOp",EDGE,"E11.20.8"),sQuery(id+"F0.wireOp",EDGE,"E11.20.9"),sQuery(id+"F0.wireOp",EDGE,"E11.21.0"),sQuery(id+"F0.wireOp",EDGE,"E11.21.1"),sQuery(id+"F0.wireOp",EDGE,"E11.21.2"),sQuery(id+"F0.wireOp",EDGE,"E11.21.3"),sQuery(id+"F0.wireOp",EDGE,"E11.21.4"),sQuery(id+"F0.wireOp",EDGE,"E11.21.5"),sQuery(id+"F0.wireOp",EDGE,"E11.21.6"),sQuery(id+"F0.wireOp",EDGE,"E11.21.7"),sQuery(id+"F0.wireOp",EDGE,"E11.21.8"),sQuery(id+"F0.wireOp",EDGE,"E11.21.9"),sQuery(id+"F0.wireOp",EDGE,"E11.22.0"),sQuery(id+"F0.wireOp",EDGE,"E11.22.1"),sQuery(id+"F0.wireOp",EDGE,"E11.22.2"),sQuery(id+"F0.wireOp",EDGE,"E11.22.3"),sQuery(id+"F0.wireOp",EDGE,"E11.22.4"),sQuery(id+"F0.wireOp",EDGE,"E11.22.5"),sQuery(id+"F0.wireOp",EDGE,"E11.22.6"),sQuery(id+"F0.wireOp",EDGE,"E11.22.7"),sQuery(id+"F0.wireOp",EDGE,"E11.22.8"),sQuery(id+"F0.wireOp",EDGE,"E11.22.9"),sQuery(id+"F0.wireOp",EDGE,"E11.23.0"),sQuery(id+"F0.wireOp",EDGE,"E11.23.1"),sQuery(id+"F0.wireOp",EDGE,"E11.23.2"),sQuery(id+"F0.wireOp",EDGE,"E11.23.3"),sQuery(id+"F0.wireOp",EDGE,"E11.23.4"),sQuery(id+"F0.wireOp",EDGE,"E11.23.5"),sQuery(id+"F0.wireOp",EDGE,"E11.23.6"),sQuery(id+"F0.wireOp",EDGE,"E11.23.7"),sQuery(id+"F0.wireOp",EDGE,"E11.23.8"),sQuery(id+"F0.wireOp",EDGE,"E11.23.9"),sQuery(id+"F0.wireOp",EDGE,"E11.24.0"),sQuery(id+"F0.wireOp",EDGE,"E11.24.1"),sQuery(id+"F0.wireOp",EDGE,"E11.24.2"),sQuery(id+"F0.wireOp",EDGE,"E11.24.3"),sQuery(id+"F0.wireOp",EDGE,"E11.24.4"),sQuery(id+"F0.wireOp",EDGE,"E11.24.5"),sQuery(id+"F0.wireOp",EDGE,"E11.24.6"),sQuery(id+"F0.wireOp",EDGE,"E11.24.7"),sQuery(id+"F0.wireOp",EDGE,"E11.24.8"),sQuery(id+"F0.wireOp",EDGE,"E11.24.9"),sQuery(id+"F0.wireOp",EDGE,"E11.25.0"),sQuery(id+"F0.wireOp",EDGE,"E11.25.1"),sQuery(id+"F0.wireOp",EDGE,"E11.25.2"),sQuery(id+"F0.wireOp",EDGE,"E11.25.3"),sQuery(id+"F0.wireOp",EDGE,"E11.25.4"),sQuery(id+"F0.wireOp",EDGE,"E11.25.5"),sQuery(id+"F0.wireOp",EDGE,"E11.25.6"),sQuery(id+"F0.wireOp",EDGE,"E11.25.7"),sQuery(id+"F0.wireOp",EDGE,"E11.25.8"),sQuery(id+"F0.wireOp",EDGE,"E11.25.9"),sQuery(id+"F0.wireOp",EDGE,"E11.26.0"),sQuery(id+"F0.wireOp",EDGE,"E11.26.1"),sQuery(id+"F0.wireOp",EDGE,"E11.26.2"),sQuery(id+"F0.wireOp",EDGE,"E11.26.3"),sQuery(id+"F0.wireOp",EDGE,"E11.26.4"),sQuery(id+"F0.wireOp",EDGE,"E11.26.5"),sQuery(id+"F0.wireOp",EDGE,"E11.26.6"),sQuery(id+"F0.wireOp",EDGE,"E11.26.7"),sQuery(id+"F0.wireOp",EDGE,"E11.26.8"),sQuery(id+"F0.wireOp",EDGE,"E11.26.9"),sQuery(id+"F0.wireOp",EDGE,"E11.27.0"),sQuery(id+"F0.wireOp",EDGE,"E11.27.1"),sQuery(id+"F0.wireOp",EDGE,"E11.27.2"),sQuery(id+"F0.wireOp",EDGE,"E11.27.3"),sQuery(id+"F0.wireOp",EDGE,"E11.27.4"),sQuery(id+"F0.wireOp",EDGE,"E11.27.5"),sQuery(id+"F0.wireOp",EDGE,"E11.27.6"),sQuery(id+"F0.wireOp",EDGE,"E11.27.7"),sQuery(id+"F0.wireOp",EDGE,"E11.27.8"),sQuery(id+"F0.wireOp",EDGE,"E11.27.9"),sQuery(id+"F0.wireOp",EDGE,"E11.28.0"),sQuery(id+"F0.wireOp",EDGE,"E11.28.1"),sQuery(id+"F0.wireOp",EDGE,"E11.28.2"),sQuery(id+"F0.wireOp",EDGE,"E11.28.3"),sQuery(id+"F0.wireOp",EDGE,"E11.28.4"),sQuery(id+"F0.wireOp",EDGE,"E11.28.5"),sQuery(id+"F0.wireOp",EDGE,"E11.28.6"),sQuery(id+"F0.wireOp",EDGE,"E11.28.7"),sQuery(id+"F0.wireOp",EDGE,"E11.28.8"),sQuery(id+"F0.wireOp",EDGE,"E11.28.9"),sQuery(id+"F0.wireOp",EDGE,"E11.29.0"),sQuery(id+"F0.wireOp",EDGE,"E11.29.1"),sQuery(id+"F0.wireOp",EDGE,"E11.29.2"),sQuery(id+"F0.wireOp",EDGE,"E11.29.3"),sQuery(id+"F0.wireOp",EDGE,"E11.29.4"),sQuery(id+"F0.wireOp",EDGE,"E11.29.5"),sQuery(id+"F0.wireOp",EDGE,"E11.29.6"),sQuery(id+"F0.wireOp",EDGE,"E11.29.7"),sQuery(id+"F0.wireOp",EDGE,"E11.29.8"),sQuery(id+"F0.wireOp",EDGE,"E11.29.9"),sQuery(id+"F0.wireOp",EDGE,"E12.trimOffspring"),sQuery(id+"F0.wireOp",EDGE,"E13.trimOffspring"),sQuery(id+"F0.wireOp",EDGE,"E14.trimOffspring"),sQuery(id+"F0.wireOp",EDGE,"E15.trimOffspring"),sQuery(id+"F0.wireOp",EDGE,"E16.trimOffspring"),sQuery(id+"F0.wireOp",EDGE,"E17.trimOffspring"),sQuery(id+"F0.wireOp",EDGE,"E18.trimOffspring"),sQuery(id+"F0.wireOp",EDGE,"E19.trimOffspring"),sQuery(id+"F0.wireOp",EDGE,"E20.trimOffspring"),sQuery(id+"F0.wireOp",EDGE,"E21.trimOffspring"),sQuery(id+"F0.wireOp",EDGE,"E22.trimOffspring"),sQuery(id+"F0.wireOp",EDGE,"E23.trimOffspring"),sQuery(id+"F0.wireOp",EDGE,"E24.trimOffspring"),sQuery(id+"F0.wireOp",EDGE,"E25.trimOffspring"),sQuery(id+"F0.wireOp",EDGE,"E26.trimOffspring"),sQuery(id+"F0.wireOp",EDGE,"E27.trimOffspring"),sQuery(id+"F0.wireOp",EDGE,"E28.trimOffspring"),sQuery(id+"F0.wireOp",EDGE,"E29.trimOffspring"),sQuery(id+"F0.wireOp",EDGE,"E30.trimOffspring"),sQuery(id+"F0.wireOp",EDGE,"E31.trimOffspring"),sQuery(id+"F0.wireOp",EDGE,"E32.trimOffspring"),sQuery(id+"F0.wireOp",EDGE,"E33.trimOffspring"),sQuery(id+"F0.wireOp",EDGE,"E34.trimOffspring"),sQuery(id+"F0.wireOp",EDGE,"E35.trimOffspring"),sQuery(id+"F0.wireOp",EDGE,"E36.trimOffspring"),sQuery(id+"F0.wireOp",EDGE,"E37.trimOffspring"),sQuery(id+"F0.wireOp",EDGE,"E38.trimOffspring"),sQuery(id+"F0.wireOp",EDGE,"E39.trimOffspring"),sQuery(id+"F0.wireOp",EDGE,"E40.trimOffspring"),sQuery(id+"F0.wireOp",EDGE,"E41")])],"isStart":false});
            var sketch = newSketch(context, id + "F2", { "sketchPlane" : qUnion([Q0])});
            skCircle(sketch, "E42", {"center": v(0, 0) * mm, "radius": 6.35 * mm});
            skCircle(sketch, "E43", {"center": v(0, 0) * mm, "radius": 12.7 * mm});
            skSolve(sketch);
        }
        {
            var Q0;
            Q0 = qSketchRegion(id + "F2", true);
            extrude(context, id + "F3", {"entities" : qUnion([Q0]), "operationType" : NewBodyOperationType.ADD, "depth" : 12.7 * mm});
        }
    });
